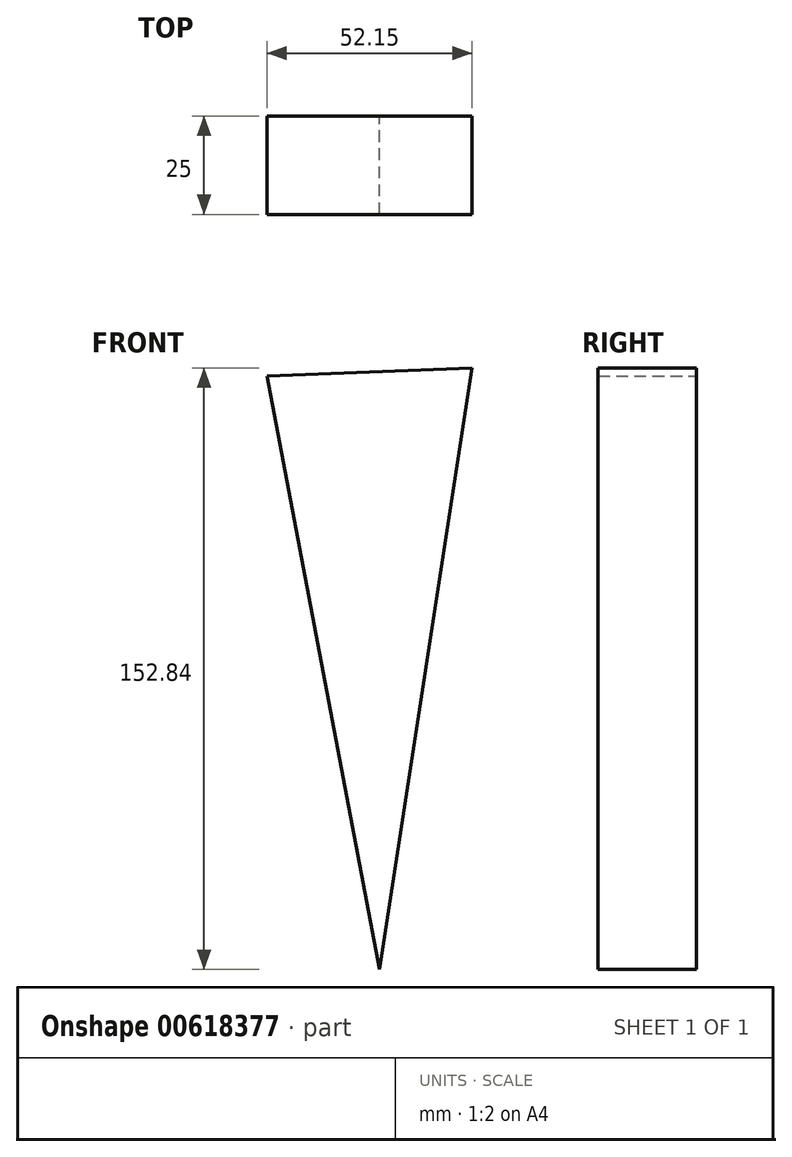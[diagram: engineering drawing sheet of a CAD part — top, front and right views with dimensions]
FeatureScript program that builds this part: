
annotation { "Feature Type Name" : "Feature", "Feature Type Description" : "" }
export const myFeature = defineFeature(function(context is Context, id is Id, definition is map)
    precondition{}
    {
        {
            var Q0;
            Q0=qCreatedBy(makeId("Front.planeOp"),FACE);
            var sketch = newSketch(context, id + "F0", { "sketchPlane" : qUnion([Q0])});
            skCircle(sketch, "E0.cCircle", {"center": v(212.44, 17.53) * mm, "radius": 50.29 * mm, "construction": true});
            skLineSegment(sketch, "E0.0", {"start": v(216.77, -82.96) * mm, "end": v(123.24, 64.02) * mm});
            skLineSegment(sketch, "E0.1", {"start": v(123.24, 64.02) * mm, "end": v(297.3, 71.53) * mm});
            skLineSegment(sketch, "E0.2", {"start": v(297.3, 71.53) * mm, "end": v(216.77, -82.96) * mm});
            skPoint(sketch, "E0.0.midPoint", {"position": v(170, -9.47) * mm});
            skSolve(sketch);
        }
        {
            var Q0;
            Q0=makeQuery(id+"F0.imprint","IMPRINT",FACE,{"disambiguationData":[TD([[makeQuery(id+"F0.imprint","IMPRINT",EDGE,{"derivedFrom":sQuery(id+"F0.wireOp",EDGE,"E0.0")}),-1.0]])]});
            var sketch = newSketch(context, id + "F1", { "sketchPlane" : qUnion([Q0])});
            skLineSegment(sketch, "E1", {"start": v(216.43, -83.28) * mm, "end": v(240.04, 69.56) * mm});
            skLineSegment(sketch, "E2", {"start": v(216.43, -83.28) * mm, "end": v(187.9, 67.52) * mm});
            skLineSegment(sketch, "E3", {"start": v(187.9, 67.52) * mm, "end": v(240.04, 69.56) * mm});
            skSolve(sketch);
        }
        {
            var Q0;
            Q0 = qSketchRegion(id + "F1", true);
            extrude(context, id + "F2", {"entities" : qUnion([Q0]), "depth" : 25 * mm, "offsetDistance" : 25 * mm});
        }
    });
